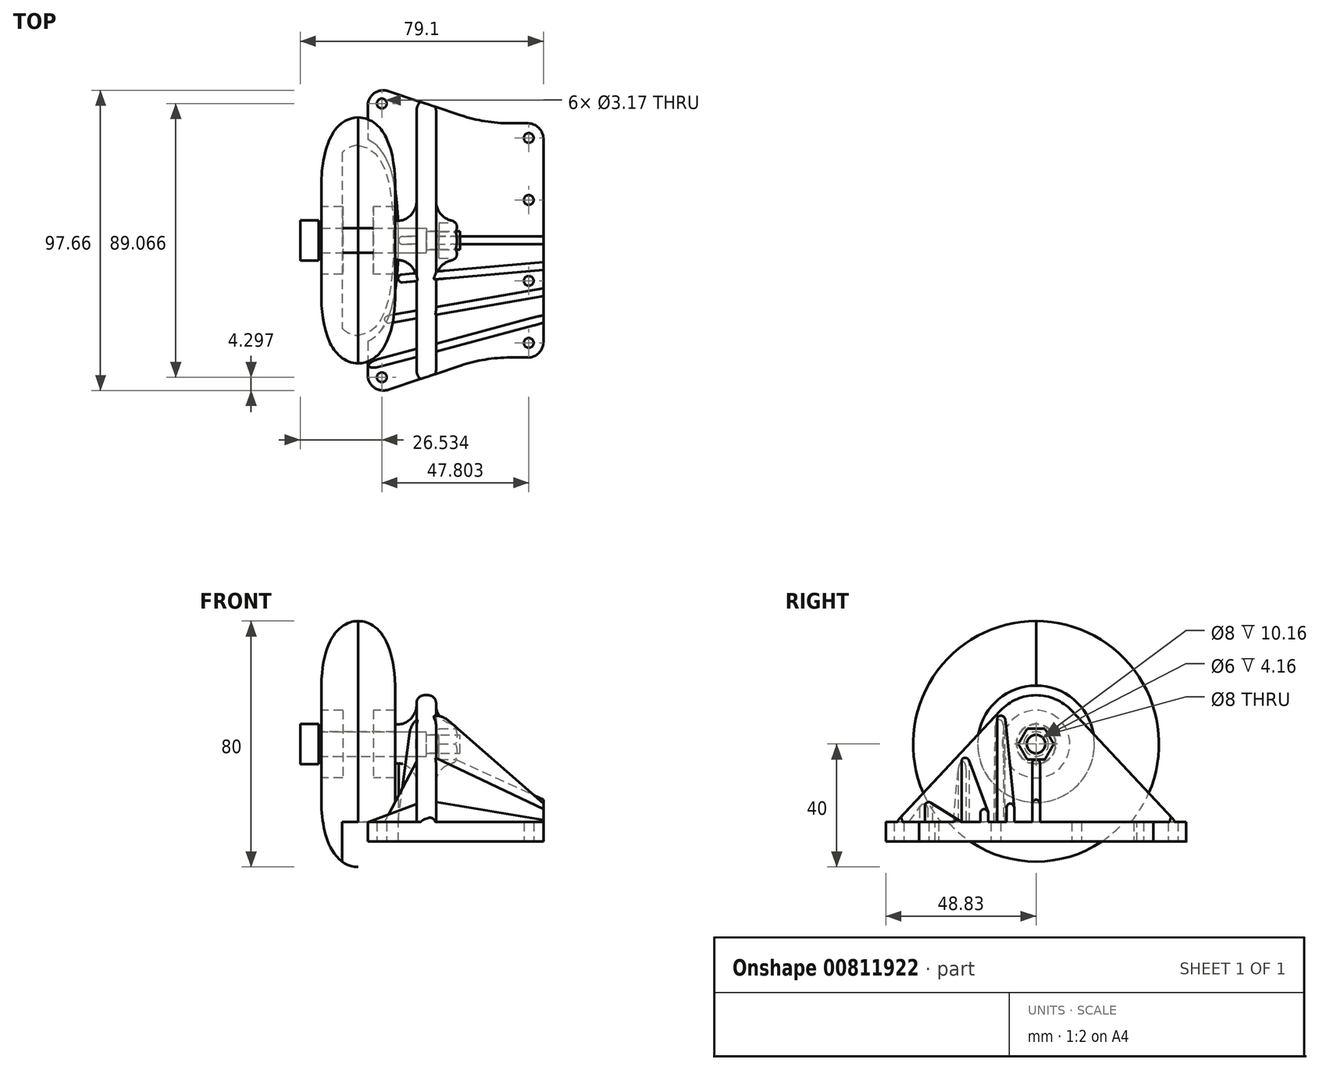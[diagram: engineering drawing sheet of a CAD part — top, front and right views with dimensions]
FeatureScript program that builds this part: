
annotation { "Feature Type Name" : "Feature", "Feature Type Description" : "" }
export const myFeature = defineFeature(function(context is Context, id is Id, definition is map)
    precondition{}
    {
        {
            var Q0;
            Q0=qCreatedBy(makeId("Top.planeOp"),FACE);
            var sketch = newSketch(context, id + "F0", { "sketchPlane" : qUnion([Q0])});
            skLineSegment(sketch, "E0", {"start": v(-19.05, 50.8) * mm, "end": v(-19.05, -50.8) * mm});
            skLineSegment(sketch, "E1", {"start": v(-19.05, -50.8) * mm, "end": v(19.05, -38.1) * mm});
            skLineSegment(sketch, "E2", {"start": v(38.1, -31.75) * mm, "end": v(38.1, 31.75) * mm});
            skLineSegment(sketch, "E3", {"start": v(19.05, 38.1) * mm, "end": v(-19.05, 50.8) * mm});
            skLineSegment(sketch, "E4", {"start": v(19.05, 38.1) * mm, "end": v(38.1, 38.1) * mm});
            skLineSegment(sketch, "E5", {"start": v(38.1, 38.1) * mm, "end": v(38.1, 31.75) * mm});
            skLineSegment(sketch, "E6", {"start": v(19.05, -38.1) * mm, "end": v(38.1, -38.1) * mm});
            skLineSegment(sketch, "E7", {"start": v(38.1, -38.1) * mm, "end": v(38.1, -31.75) * mm});
            skSolve(sketch);
        }
        {
            var Q0;
            Q0=makeQuery(id+"F0.imprint","IMPRINT",FACE,{"disambiguationData":[TD([[makeQuery(id+"F0.imprint","IMPRINT",EDGE,{"derivedFrom":sQuery(id+"F0.wireOp",EDGE,"E0")}),1.0]])]});
            extrude(context, id + "F1", {"entities" : qUnion([Q0]), "depth" : 6.35 * mm});
        }
        {
            var Q0;
            Q0=makeQuery(id+"F1.opExtrude","CAP_FACE",FACE,{"disambiguationData":[OSD([sQuery(id+"F0.wireOp",EDGE,"E0"),sQuery(id+"F0.wireOp",EDGE,"E1"),sQuery(id+"F0.wireOp",EDGE,"E2"),sQuery(id+"F0.wireOp",EDGE,"E3")])],"isStart":false});
            var sketch = newSketch(context, id + "F2", { "sketchPlane" : qUnion([Q0])});
            skLineSegment(sketch, "E8", {"start": v(-3.18, 45.5) * mm, "end": v(-3.17, -45.5) * mm});
            skLineSegment(sketch, "E9", {"start": v(-3.17, -45.5) * mm, "end": v(3.18, -43.4) * mm});
            skLineSegment(sketch, "E10", {"start": v(3.18, -43.4) * mm, "end": v(3.17, 43.4) * mm});
            skLineSegment(sketch, "E11", {"start": v(3.17, 43.4) * mm, "end": v(-3.18, 45.5) * mm});
            skSolve(sketch);
        }
        {
            var Q0;
            Q0=makeQuery(id+"F2.imprint","IMPRINT",FACE,{"disambiguationData":[TD([[makeQuery(id+"F2.imprint","IMPRINT",EDGE,{"derivedFrom":sQuery(id+"F2.wireOp",EDGE,"E8")}),1.0]])]});
            extrude(context, id + "F3", {"entities" : qUnion([Q0]), "operationType" : NewBodyOperationType.ADD, "depth" : 50.8 * mm, "offsetDistance" : 25.4 * mm});
        }
        {
            var Q0;
            Q0=qCreatedBy(makeId("Right.planeOp"),FACE);
            var sketch = newSketch(context, id + "F4", { "sketchPlane" : qUnion([Q0])});
            skArc(sketch, "E12", {"start": v(11.6, 42.6) * mm, "mid": v(0, 47.62) * mm, "end": v(-11.6, 42.6) * mm});
            skLineSegment(sketch, "E13", {"start": v(11.6, 42.6) * mm, "end": v(45.5, 6.35) * mm});
            skLineSegment(sketch, "E14", {"start": v(-11.6, 42.6) * mm, "end": v(-45.5, 6.35) * mm});
            skLineSegment(sketch, "E15", {"start": v(45.5, 6.35) * mm, "end": v(53.44, 6.35) * mm});
            skLineSegment(sketch, "E16", {"start": v(53.44, 6.35) * mm, "end": v(53.44, 59.99) * mm});
            skLineSegment(sketch, "E17", {"start": v(53.44, 59.99) * mm, "end": v(-55.67, 59.99) * mm});
            skLineSegment(sketch, "E18", {"start": v(-55.67, 59.99) * mm, "end": v(-55.67, 6.35) * mm});
            skLineSegment(sketch, "E19", {"start": v(-55.67, 6.35) * mm, "end": v(-45.5, 6.35) * mm});
            skSolve(sketch);
        }
        {
            var Q0;
            Q0=makeQuery(id+"F4.imprint","IMPRINT",FACE,{"disambiguationData":[TD([[makeQuery(id+"F4.imprint","IMPRINT",EDGE,{"derivedFrom":sQuery(id+"F4.wireOp",EDGE,"E12")}),-1.0]])]});
            extrude(context, id + "F5", {"entities" : qUnion([Q0]), "operationType" : NewBodyOperationType.REMOVE, "oppositeDirection" : true, "depth" : 7.11 * mm, "hasSecondDirection" : true, "secondDirectionOppositeDirection" : false, "secondDirectionDepth" : 4.06 * mm});
        }
        {
            var Q0;
            Q0=qCreatedBy(makeId("Right.planeOp"),FACE);
            var sketch = newSketch(context, id + "F6", { "sketchPlane" : qUnion([Q0])});
            skCircle(sketch, "E20", {"center": v(0, 513) * mm, "radius": 63.5 * mm});
            skCircle(sketch, "E21", {"center": v(0, 31.75) * mm, "radius": 6.35 * mm});
            skSolve(sketch);
        }
        {
            var Q0;
            Q0=qSketchRegion(id+"F6",true);
            extrude(context, id + "F7", {"entities" : qUnion([Q0]), "operationType" : NewBodyOperationType.ADD, "depth" : 10.16 * mm, "hasSecondDirection" : true, "secondDirectionOppositeDirection" : true, "secondDirectionDepth" : 10.16 * mm});
        }
        {
            var Q0;
            Q0=makeQuery(id+"F7.boolean.opBoolean","INTERSECT",EDGE,{"derivedFrom":[makeQuery(id+"F3.opExtrude","SWEPT_FACE",FACE,{"disambiguationData":[OSD([sQuery(id+"F2.wireOp",EDGE,"E8")])]}),makeQuery(id+"F7.opExtrude","SWEPT_FACE",FACE,{"disambiguationData":[OSD([sQuery(id+"F6.wireOp",EDGE,"E21")])]})]});
            var Q1;
            Q1=makeQuery(id+"F7.boolean.opBoolean","INTERSECT",EDGE,{"derivedFrom":[makeQuery(id+"F3.opExtrude","SWEPT_FACE",FACE,{"disambiguationData":[OSD([sQuery(id+"F2.wireOp",EDGE,"E10")])]}),makeQuery(id+"F7.opExtrude","SWEPT_FACE",FACE,{"disambiguationData":[OSD([sQuery(id+"F6.wireOp",EDGE,"E21")])]})]});
            fillet(context, id + "F8", {"entities" : qUnion([Q0, Q1]), "radius" : 6.35 * mm, "tangentPropagation" : true, "allowEdgeOverflow" : false});
        }
        {
            var Q0;
            Q0=makeQuery(id+"F5.boolean.opBoolean","INTERSECT",EDGE,{"derivedFrom":[makeQuery(id+"F3.opExtrude","SWEPT_FACE",FACE,{"disambiguationData":[OSD([sQuery(id+"F2.wireOp",EDGE,"E8")])]}),makeQuery(id+"F5.opExtrude","SWEPT_FACE",FACE,{"disambiguationData":[OSD([sQuery(id+"F4.wireOp",EDGE,"E13")])]})]});
            var Q1;
            Q1=makeQuery(id+"F5.boolean.opBoolean","INTERSECT",EDGE,{"derivedFrom":[makeQuery(id+"F3.opExtrude","SWEPT_FACE",FACE,{"disambiguationData":[OSD([sQuery(id+"F2.wireOp",EDGE,"E10")])]}),makeQuery(id+"F5.opExtrude","SWEPT_FACE",FACE,{"disambiguationData":[OSD([sQuery(id+"F4.wireOp",EDGE,"E13")])]})]});
            fillet(context, id + "F9", {"entities" : qUnion([Q0, Q1]), "radius" : 2.54 * mm, "tangentPropagation" : true, "allowEdgeOverflow" : false});
        }
        {
            var Q0;
            Q0=qCreatedBy(makeId("Right.planeOp"),FACE);
            var sketch = newSketch(context, id + "F10", { "sketchPlane" : qUnion([Q0])});
            skCircle(sketch, "E22", {"center": v(0, 31.75) * mm, "radius": 4 * mm});
            skSolve(sketch);
        }
        {
            var Q0;
            Q0=qSketchRegion(id+"F10",true);
            extrude(context, id + "F11", {"entities" : qUnion([Q0]), "operationType" : NewBodyOperationType.REMOVE, "oppositeDirection" : true, "depth" : 25.4 * mm});
        }
        {
            var Q0;
            Q0=makeQuery(id+"F7.opExtrude","CAP_FACE",FACE,{"disambiguationData":[OSD([sQuery(id+"F6.wireOp",EDGE,"E21")])],"isStart":false});
            var sketch = newSketch(context, id + "F12", { "sketchPlane" : qUnion([Q0])});
            skCircle(sketch, "E23.cCircle", {"center": v(0, 31.75) * mm, "radius": 5 * mm, "construction": true});
            skLineSegment(sketch, "E23.0", {"start": v(-2.89, 36.75) * mm, "end": v(2.89, 36.75) * mm});
            skLineSegment(sketch, "E23.1", {"start": v(2.89, 36.75) * mm, "end": v(5.77, 31.75) * mm});
            skLineSegment(sketch, "E23.2", {"start": v(5.77, 31.75) * mm, "end": v(2.89, 26.75) * mm});
            skLineSegment(sketch, "E23.3", {"start": v(2.89, 26.75) * mm, "end": v(-2.89, 26.75) * mm});
            skLineSegment(sketch, "E23.4", {"start": v(-2.89, 26.75) * mm, "end": v(-5.77, 31.75) * mm});
            skLineSegment(sketch, "E23.5", {"start": v(-5.77, 31.75) * mm, "end": v(-2.89, 36.75) * mm});
            skPoint(sketch, "E23.0.midPoint", {"position": v(0, 36.75) * mm});
            skSolve(sketch);
        }
        {
            var Q0;
            Q0=makeQuery(id+"F12.imprint","IMPRINT",FACE,{"disambiguationData":[TD([[makeQuery(id+"F12.imprint","IMPRINT",EDGE,{"derivedFrom":sQuery(id+"F12.wireOp",EDGE,"E23.0")}),-1.0]])]});
            extrude(context, id + "F13", {"entities" : qUnion([Q0]), "operationType" : NewBodyOperationType.REMOVE, "oppositeDirection" : true, "depth" : 6 * mm});
        }
        {
            var Q0;
            Q0=makeQuery(id+"F7.opExtrude","CAP_EDGE",EDGE,{"disambiguationData":[OSD([sQuery(id+"F6.wireOp",EDGE,"E21")])],"isStart":false});
            fillet(context, id + "F14", {"entities" : qUnion([Q0]), "radius" : 2.54 * mm, "tangentPropagation" : true, "allowEdgeOverflow" : false});
        }
        {
            var Q0;
            Q0=makeQuery(id+"F7.opExtrude","SWEPT_BODY",BODY,{"disambiguationData":[OSD([sQuery(id+"F6.wireOp",EDGE,"E20")])]});
            deleteBodies(context, id + "F15", {"entities" : qUnion([Q0])});
        }
        {
            var Q0;
            Q0=qCreatedBy(makeId("Right.planeOp"),FACE);
            var sketch = newSketch(context, id + "F16", { "sketchPlane" : qUnion([Q0])});
            skCircle(sketch, "E24", {"center": v(0, 31.75) * mm, "radius": 3 * mm});
            skSolve(sketch);
        }
        {
            var Q0;
            Q0=qSketchRegion(id+"F16",true);
            extrude(context, id + "F17", {"entities" : qUnion([Q0]), "operationType" : NewBodyOperationType.REMOVE, "depth" : 25.4 * mm});
        }
        {
            var Q0;
            Q0=qCreatedBy(makeId("Front.planeOp"),FACE);
            var sketch = newSketch(context, id + "F18", { "sketchPlane" : qUnion([Q0])});
            skLineSegment(sketch, "E25", {"start": v(0, 31.75) * mm, "end": v(-46.53, 31.75) * mm, "construction": true});
            skLineSegment(sketch, "E26", {"start": v(-35, 35.75) * mm, "end": v(0, 35.75) * mm});
            skLineSegment(sketch, "E27", {"start": v(0, 35.75) * mm, "end": v(0, 34.75) * mm});
            skLineSegment(sketch, "E28", {"start": v(0, 34.75) * mm, "end": v(11, 34.75) * mm});
            skLineSegment(sketch, "E29", {"start": v(11, 34.75) * mm, "end": v(11, 31.75) * mm});
            skLineSegment(sketch, "E30", {"start": v(11, 31.75) * mm, "end": v(-41, 31.75) * mm});
            skLineSegment(sketch, "E31", {"start": v(-35, 35.75) * mm, "end": v(-35, 38.25) * mm});
            skLineSegment(sketch, "E32", {"start": v(-35, 38.25) * mm, "end": v(-41, 38.25) * mm});
            skLineSegment(sketch, "E33", {"start": v(-41, 38.25) * mm, "end": v(-41, 31.75) * mm});
            skSolve(sketch);
        }
        {
            var Q0;
            Q0=makeQuery(id+"F18.imprint","IMPRINT",FACE,{"disambiguationData":[TD([[makeQuery(id+"F18.imprint","IMPRINT",EDGE,{"derivedFrom":sQuery(id+"F18.wireOp",EDGE,"E26")}),-1.0]])]});
            var Q1;
            Q1=sQuery(id+"F18.wireOp",EDGE,"E25");
            revolve(context, id + "F19", {"entities" : qUnion([Q0]), "axis" : qUnion([Q1]), "revolveType" : RevolveType.FULL});
        }
        {
            var Q0;
            Q0=qCreatedBy(makeId("Front.planeOp"),FACE);
            var sketch = newSketch(context, id + "F20", { "sketchPlane" : qUnion([Q0])});
            skLineSegment(sketch, "E34", {"start": v(-51.26, 31.75) * mm, "end": v(0, 31.75) * mm});
            skLineSegment(sketch, "E35", {"start": v(-22.16, 31.75) * mm, "end": v(-22.16, 71.75) * mm, "construction": true});
            skPoint(sketch, "E36", {"position": v(-25.63, 31.75) * mm});
            skLineSegment(sketch, "E37", {"start": v(-22.16, 35.75) * mm, "end": v(-10.16, 35.75) * mm});
            skLineSegment(sketch, "E38", {"start": v(-10.16, 35.75) * mm, "end": v(-10.16, 50.75) * mm});
            skPoint(sketch, "E39.MirrorCS.2.internal.orphan", {"position": v(-34.16, 31.75) * mm});
            skPoint(sketch, "E39.MirrorCS.start.orphan", {"position": v(-22.16, 71.75) * mm});
            skPoint(sketch, "E40.2.internal.orphan", {"position": v(-10.16, 31.75) * mm});
            skFitSpline(sketch, "E41", {"points": [v(-22.16, 71.75) * mm, v(-10.16, 50.75) * mm], "startDerivative": vector(15.26, -0.07) * mm, "endDerivative": vector(1.21, -49.43) * mm});
            skPoint(sketch, "E42.MirrorCS.end.orphan", {"position": v(-34.16, 50.75) * mm});
            skFitSpline(sketch, "E43.MirrorCS", {"points": [v(-22.16, 71.75) * mm, v(-34.16, 50.75) * mm], "startDerivative": vector(-15.26, -0.07) * mm, "endDerivative": vector(-1.21, -49.43) * mm});
            skLineSegment(sketch, "E44.MirrorCS", {"start": v(-34.16, 35.75) * mm, "end": v(-34.16, 50.75) * mm});
            skLineSegment(sketch, "E45.MirrorCS", {"start": v(-22.16, 35.75) * mm, "end": v(-34.16, 35.75) * mm});
            skSolve(sketch);
        }
        {
            var Q0;
            Q0=makeQuery(id+"F20.imprint","IMPRINT",FACE,{"disambiguationData":[TD([[makeQuery(id+"F20.imprint","IMPRINT",EDGE,{"derivedFrom":sQuery(id+"F20.wireOp",EDGE,"E37")}),1.0]])]});
            var Q1;
            Q1=sQuery(id+"F20.wireOp",EDGE,"E34");
            revolve(context, id + "F21", {"entities" : qUnion([Q0]), "axis" : qUnion([Q1]), "revolveType" : RevolveType.FULL});
        }
        {
            var Q0;
            Q0=qCreatedBy(makeId("Front.planeOp"),FACE);
            var sketch = newSketch(context, id + "F22", { "sketchPlane" : qUnion([Q0])});
            skLineSegment(sketch, "E46", {"start": v(-62.06, 31.75) * mm, "end": v(0, 31.75) * mm, "construction": true});
            skLineSegment(sketch, "E47", {"start": v(-10.16, 31.75) * mm, "end": v(-10.16, 42.75) * mm});
            skLineSegment(sketch, "E48", {"start": v(-10.16, 42.75) * mm, "end": v(-17.16, 42.75) * mm});
            skLineSegment(sketch, "E49", {"start": v(-17.16, 42.75) * mm, "end": v(-17.16, 31.75) * mm});
            skLineSegment(sketch, "E50", {"start": v(-17.16, 31.75) * mm, "end": v(-10.16, 31.75) * mm});
            skLineSegment(sketch, "E51", {"start": v(-22.16, 31.75) * mm, "end": v(-22.16, 46.12) * mm, "construction": true});
            skLineSegment(sketch, "E52.MirrorCS", {"start": v(-34.16, 42.75) * mm, "end": v(-27.16, 42.75) * mm});
            skLineSegment(sketch, "E53.MirrorCS", {"start": v(-27.16, 42.75) * mm, "end": v(-27.16, 31.75) * mm});
            skLineSegment(sketch, "E54.MirrorCS", {"start": v(-34.16, 31.75) * mm, "end": v(-34.16, 42.75) * mm});
            skLineSegment(sketch, "E55", {"start": v(-27.16, 31.75) * mm, "end": v(-34.16, 31.75) * mm});
            skSolve(sketch);
        }
        {
            var Q0;
            Q0=qSketchRegion(id+"F22",true);
            var Q1;
            Q1=sQuery(id+"F22.wireOp",EDGE,"E46");
            revolve(context, id + "F23", {"entities" : qUnion([Q0]), "axis" : qUnion([Q1]), "revolveType" : RevolveType.FULL});
        }
        {
            var Q0;
            {var subQ0=sQuery(id+"F0.wireOp",EDGE,"E3");var subQ1=sQuery(id+"F0.wireOp",EDGE,"E1");var subQ2=sQuery(id+"F0.wireOp",EDGE,"E0");Q0=makeQuery(id+"F3.boolean.opBoolean","SPLIT",FACE,{"disambiguationData":[TD([makeQuery(id+"F1.opExtrude","SWEPT_FACE",FACE,{"disambiguationData":[OSD([subQ2])]})])],"derivedFrom":makeQuery(id+"F1.opExtrude","CAP_FACE",FACE,{"disambiguationData":[OSD([subQ2,subQ1,sQuery(id+"F0.wireOp",EDGE,"E2"),subQ0])],"isStart":false})});}
            var sketch = newSketch(context, id + "F24", { "sketchPlane" : qUnion([Q0])});
            skLineSegment(sketch, "E56", {"start": v(-19.05, 32.85) * mm, "end": v(-19.05, -32.85) * mm});
            skFitSpline(sketch, "E57.0", {"points": [v(-22.67, -33.39) * mm, v(-22.46, -33.43) * mm, v(-22.05, -33.49) * mm, v(-21.48, -33.49) * mm, v(-20.97, -33.44) * mm, v(-20.5, -33.35) * mm, v(-20.07, -33.24) * mm, v(-19.65, -33.1) * mm, v(-19.27, -32.95) * mm, v(-18.9, -32.79) * mm, v(-18.56, -32.62) * mm, v(-18.23, -32.43) * mm, v(-17.91, -32.24) * mm, v(-17.5, -31.97) * mm, v(-17.03, -31.62) * mm, v(-16.3, -31.03) * mm, v(-15.49, -30.22) * mm, v(-14.62, -29.2) * mm, v(-13.87, -28.1) * mm, v(-13.21, -26.98) * mm, v(-12.65, -25.84) * mm, v(-12.17, -24.7) * mm, v(-11.76, -23.55) * mm, v(-11.28, -22.02) * mm, v(-10.8, -20.12) * mm, v(-10.34, -17.83) * mm, v(-10, -15.56) * mm, v(-9.63, -12.57) * mm, v(-9.33, -8.85) * mm, v(-9.13, -4.4) * mm, v(-9.07, 0.02) * mm, v(-9.13, 4.46) * mm, v(-9.3, 8.17) * mm, v(-9.52, 11.16) * mm, v(-9.73, 13.4) * mm, v(-10, 15.66) * mm, v(-10.36, 17.92) * mm, v(-10.81, 20.2) * mm, v(-11.4, 22.47) * mm, v(-12.03, 24.37) * mm, v(-12.67, 25.89) * mm, v(-13.24, 27.03) * mm, v(-13.9, 28.15) * mm, v(-14.65, 29.23) * mm, v(-15.52, 30.26) * mm, v(-16.5, 31.2) * mm, v(-17.6, 32.06) * mm, v(-18.66, 32.7) * mm, v(-19.65, 33.11) * mm, v(-20.35, 33.32) * mm, v(-20.98, 33.44) * mm, v(-21.49, 33.49) * mm, v(-22.05, 33.48) * mm, v(-22.46, 33.43) * mm, v(-22.67, 33.39) * mm]});
            skPoint(sketch, "E58.trimOffspring.end.orphan", {"position": v(-22.16, 30.9) * mm});
            skPoint(sketch, "E59.start.orphan", {"position": v(-22.16, -30.9) * mm});
            skLineSegment(sketch, "E60", {"start": v(-19.05, 32.85) * mm, "end": v(-27.36, 32.85) * mm});
            skLineSegment(sketch, "E61", {"start": v(-27.36, 32.85) * mm, "end": v(-27.36, -33.81) * mm});
            skLineSegment(sketch, "E62", {"start": v(-27.36, -33.81) * mm, "end": v(-19.05, -32.85) * mm});
            skSolve(sketch);
        }
        {
            var Q0;
            Q0=makeQuery(id+"F24.imprint","IMPRINT",FACE,{"disambiguationData":[TD([[makeQuery(id+"F24.imprint","IMPRINT",EDGE,{"derivedFrom":sQuery(id+"F24.wireOp",EDGE,"E56")}),-1.0]])]});
            var Q1;
            Q1=makeQuery(id+"F24.imprint","IMPRINT",FACE,{"disambiguationData":[TD([[makeQuery(id+"F24.imprint","IMPRINT",EDGE,{"derivedFrom":sQuery(id+"F24.wireOp",EDGE,"E56")}),1.0]])]});
            extrude(context, id + "F25", {"entities" : qUnion([Q0, Q1]), "operationType" : NewBodyOperationType.REMOVE, "oppositeDirection" : true, "depth" : 25.4 * mm});
        }
        {
            var Q0;
            Q0=qCreatedBy(makeId("Front.planeOp"),FACE);
            var sketch = newSketch(context, id + "F26", { "sketchPlane" : qUnion([Q0])});
            skLineSegment(sketch, "E63", {"start": v(-9.01, 6.35) * mm, "end": v(-9.01, 26.67) * mm});
            skLineSegment(sketch, "E64", {"start": v(-9.01, 26.67) * mm, "end": v(9.85, 26.67) * mm});
            skLineSegment(sketch, "E65", {"start": v(9.85, 26.67) * mm, "end": v(53.98, 6.35) * mm});
            skLineSegment(sketch, "E66", {"start": v(53.98, 6.35) * mm, "end": v(-9.01, 6.35) * mm});
            skSolve(sketch);
        }
        {
            var Q0;
            Q0=makeQuery(id+"F26.imprint","IMPRINT",FACE,{"disambiguationData":[TD([[makeQuery(id+"F26.imprint","IMPRINT",EDGE,{"derivedFrom":sQuery(id+"F26.wireOp",EDGE,"E63")}),-1.0]])]});
            extrude(context, id + "F27", {"entities" : qUnion([Q0]), "operationType" : NewBodyOperationType.ADD, "depth" : 1.27 * mm, "hasSecondDirection" : true, "secondDirectionOppositeDirection" : true, "secondDirectionDepth" : 1.27 * mm});
        }
        {
            var Q0;
            Q0=qCreatedBy(makeId("Top.planeOp"),FACE);
            var sketch = newSketch(context, id + "F28", { "sketchPlane" : qUnion([Q0])});
            skLineSegment(sketch, "E67", {"start": v(-23.06, -52.14) * mm, "end": v(133.35, 0) * mm});
            skLineSegment(sketch, "E68", {"start": v(133.35, 0) * mm, "end": v(-28.84, 0) * mm});
            skLineSegment(sketch, "E69", {"start": v(133.35, 0) * mm, "end": v(-37.86, -14.98) * mm});
            skLineSegment(sketch, "E70", {"start": v(133.35, 0) * mm, "end": v(-37.54, -30.13) * mm});
            skLineSegment(sketch, "E71", {"start": v(133.35, 0) * mm, "end": v(-45.99, -48.05) * mm});
            skSolve(sketch);
        }
        {
            var Q0;
            Q0=sQuery(id+"F28.wireOp",EDGE,"E69");
            cPlane(context, id + "F29", {"entities" : qUnion([Q0]), "cplaneType" : CPlaneType.LINE_ANGLE, "offset" : 25.4 * mm, "angle" : 0 * degree, "width" : 152.4 * mm, "height" : 152.4 * mm});
        }
        {
            var Q0;
            Q0=qCreatedBy(id+"F29.planeOp",FACE);
            var sketch = newSketch(context, id + "F30", { "sketchPlane" : qUnion([Q0])});
            skLineSegment(sketch, "E72", {"start": v(6.12, 39.44) * mm, "end": v(44.18, 6.35) * mm});
            skLineSegment(sketch, "E73", {"start": v(44.18, 6.35) * mm, "end": v(-10.24, 6.35) * mm});
            skLineSegment(sketch, "E74", {"start": v(-10.24, 6.35) * mm, "end": v(-6.43, 35.5) * mm});
            skPoint(sketch, "E75.visualSharp", {"position": v(-6.52, 34.82) * mm});
            skArc(sketch, "E75.filletArc", {"start": v(-3.16, 40.25) * mm, "mid": v(-5.37, 38.27) * mm, "end": v(-6.43, 35.5) * mm});
            skLineSegment(sketch, "E76", {"start": v(1.95, 41) * mm, "end": v(0.46, 41) * mm});
            skLineSegment(sketch, "E77", {"start": v(0.46, 41) * mm, "end": v(-3.16, 40.25) * mm});
            skPoint(sketch, "E78.visualSharp", {"position": v(4.32, 41) * mm});
            skArc(sketch, "E78.filletArc", {"start": v(6.12, 39.44) * mm, "mid": v(4.17, 40.6) * mm, "end": v(1.95, 41) * mm});
            skSolve(sketch);
        }
        {
            var Q0;
            Q0=makeQuery(id+"F30.imprint","IMPRINT",FACE,{"disambiguationData":[TD([[makeQuery(id+"F30.imprint","IMPRINT",EDGE,{"derivedFrom":sQuery(id+"F30.wireOp",EDGE,"E72")}),-1.0]])]});
            extrude(context, id + "F31", {"entities" : qUnion([Q0]), "operationType" : NewBodyOperationType.ADD, "depth" : 1.27 * mm, "hasSecondDirection" : true, "secondDirectionOppositeDirection" : true, "secondDirectionDepth" : 1.27 * mm});
        }
        {
            var Q0;
            Q0=sQuery(id+"F28.wireOp",EDGE,"E70");
            cPlane(context, id + "F32", {"entities" : qUnion([Q0]), "cplaneType" : CPlaneType.LINE_ANGLE, "offset" : 25.4 * mm, "angle" : 0 * degree, "width" : 152.4 * mm, "height" : 152.4 * mm});
        }
        {
            var Q0;
            Q0=qCreatedBy(id+"F32.planeOp",FACE);
            var sketch = newSketch(context, id + "F33", { "sketchPlane" : qUnion([Q0])});
            skLineSegment(sketch, "E79", {"start": v(43.53, 6.35) * mm, "end": v(-17.77, 6.35) * mm});
            skLineSegment(sketch, "E80", {"start": v(-17.77, 6.35) * mm, "end": v(-6.14, 28.2) * mm});
            skLineSegment(sketch, "E81", {"start": v(-6.14, 28.2) * mm, "end": v(-2.9, 28.2) * mm});
            skLineSegment(sketch, "E82", {"start": v(-2.9, 28.2) * mm, "end": v(43.53, 6.35) * mm});
            skSolve(sketch);
        }
        {
            var Q0;
            Q0=makeQuery(id+"F33.imprint","IMPRINT",FACE,{"disambiguationData":[TD([[makeQuery(id+"F33.imprint","IMPRINT",EDGE,{"derivedFrom":sQuery(id+"F33.wireOp",EDGE,"E79")}),-1.0]])]});
            extrude(context, id + "F34", {"entities" : qUnion([Q0]), "operationType" : NewBodyOperationType.ADD, "depth" : 1.27 * mm, "hasSecondDirection" : true, "secondDirectionOppositeDirection" : true, "secondDirectionDepth" : 1.27 * mm});
        }
        {
            var Q0;
            Q0=sQuery(id+"F28.wireOp",EDGE,"E71");
            cPlane(context, id + "F35", {"entities" : qUnion([Q0]), "cplaneType" : CPlaneType.LINE_ANGLE, "offset" : 25.4 * mm, "angle" : 0 * degree, "width" : 152.4 * mm, "height" : 152.4 * mm});
        }
        {
            var Q0;
            Q0=qCreatedBy(id+"F35.planeOp",FACE);
            var sketch = newSketch(context, id + "F36", { "sketchPlane" : qUnion([Q0])});
            skLineSegment(sketch, "E83", {"start": v(-28.7, 6.35) * mm, "end": v(-10.05, 13.08) * mm});
            skLineSegment(sketch, "E84", {"start": v(-10.05, 13.08) * mm, "end": v(-7.43, 13.08) * mm});
            skLineSegment(sketch, "E85", {"start": v(-7.43, 13.08) * mm, "end": v(34.6, 6.35) * mm});
            skLineSegment(sketch, "E86", {"start": v(34.6, 6.35) * mm, "end": v(-28.7, 6.35) * mm});
            skSolve(sketch);
        }
        {
            var Q0;
            Q0=makeQuery(id+"F36.imprint","IMPRINT",FACE,{"disambiguationData":[TD([[makeQuery(id+"F36.imprint","IMPRINT",EDGE,{"derivedFrom":sQuery(id+"F36.wireOp",EDGE,"E83")}),-1.0]])]});
            extrude(context, id + "F37", {"entities" : qUnion([Q0]), "operationType" : NewBodyOperationType.ADD, "depth" : 1.27 * mm, "hasSecondDirection" : true, "secondDirectionOppositeDirection" : true, "secondDirectionDepth" : 1.27 * mm});
        }
        {
            var Q0;
            Q0=qCreatedBy(makeId("Top.planeOp"),FACE);
            var sketch = newSketch(context, id + "F38", { "sketchPlane" : qUnion([Q0])});
            skLineSegment(sketch, "E87", {"start": v(-19.05, 47.14) * mm, "end": v(-19.05, -47.14) * mm});
            skLineSegment(sketch, "E88", {"start": v(-12.36, 48.57) * mm, "end": v(-22.52, 51.96) * mm});
            skLineSegment(sketch, "E89", {"start": v(38.1, 70.87) * mm, "end": v(38.1, -40.92) * mm});
            skLineSegment(sketch, "E90", {"start": v(-22.52, -51.96) * mm, "end": v(-12.36, -48.57) * mm});
            skPoint(sketch, "E91.visualSharp", {"position": v(-19.05, 50.8) * mm});
            skArc(sketch, "E91.filletArc", {"start": v(-19.05, 47.14) * mm, "mid": v(-20, 50.1) * mm, "end": v(-22.52, 51.96) * mm});
            skPoint(sketch, "E92.visualSharp", {"position": v(-19.05, -50.8) * mm});
            skArc(sketch, "E92.filletArc", {"start": v(-22.52, -51.96) * mm, "mid": v(-20, -50.1) * mm, "end": v(-19.05, -47.14) * mm});
            skLineSegment(sketch, "E93", {"start": v(-19.05, 43.75) * mm, "end": v(-19.05, 35.1) * mm});
            skLineSegment(sketch, "E94", {"start": v(-19.05, 35.1) * mm, "end": v(-54.33, 35.1) * mm});
            skLineSegment(sketch, "E95", {"start": v(-54.33, 35.1) * mm, "end": v(-54.33, 78.4) * mm});
            skLineSegment(sketch, "E96", {"start": v(-54.33, 78.4) * mm, "end": v(38.1, 70.87) * mm});
            skArc(sketch, "E97.filletArc", {"start": v(-12.36, 48.57) * mm, "mid": v(-16.94, 47.87) * mm, "end": v(-19.05, 43.75) * mm});
            skLineSegment(sketch, "E98", {"start": v(-19.05, -43.75) * mm, "end": v(-19.05, -36.43) * mm});
            skLineSegment(sketch, "E99", {"start": v(-19.05, -36.43) * mm, "end": v(-56.87, -36.43) * mm});
            skLineSegment(sketch, "E100", {"start": v(-56.87, -36.43) * mm, "end": v(-56.87, -71.2) * mm});
            skLineSegment(sketch, "E101", {"start": v(-56.87, -71.2) * mm, "end": v(38.1, -40.92) * mm});
            skArc(sketch, "E102.filletArc", {"start": v(-19.05, -43.75) * mm, "mid": v(-16.94, -47.87) * mm, "end": v(-12.36, -48.57) * mm});
            skSolve(sketch);
        }
        {
            var Q0;
            Q0=makeQuery(id+"F38.imprint","IMPRINT",FACE,{"disambiguationData":[TD([[makeQuery(id+"F38.imprint","IMPRINT",EDGE,{"derivedFrom":sQuery(id+"F38.wireOp",EDGE,"E87")}),1.0]])]});
            extrude(context, id + "F39", {"entities" : qUnion([Q0]), "operationType" : NewBodyOperationType.REMOVE, "depth" : 25.4 * mm});
        }
        {
            var Q0;
            Q0=qCreatedBy(makeId("Top.planeOp"),FACE);
            var sketch = newSketch(context, id + "F40", { "sketchPlane" : qUnion([Q0])});
            skCircle(sketch, "E103", {"center": v(-14.47, 44.53) * mm, "radius": 1.59 * mm});
            skCircle(sketch, "E104", {"center": v(33.34, 33.34) * mm, "radius": 1.59 * mm});
            skCircle(sketch, "E105", {"center": v(33.34, 13.15) * mm, "radius": 1.59 * mm});
            skLineSegment(sketch, "E106", {"start": v(-47.45, 0) * mm, "end": v(55.73, 0) * mm, "construction": true});
            skCircle(sketch, "E107.MirrorC", {"center": v(-14.47, -44.53) * mm, "radius": 1.59 * mm});
            skCircle(sketch, "E108.MirrorC", {"center": v(33.34, -33.34) * mm, "radius": 1.59 * mm});
            skCircle(sketch, "E109.MirrorC", {"center": v(33.34, -13.15) * mm, "radius": 1.59 * mm});
            skSolve(sketch);
        }
        {
            var Q0;
            Q0=qSketchRegion(id+"F40",true);
            extrude(context, id + "F41", {"entities" : qUnion([Q0]), "operationType" : NewBodyOperationType.REMOVE, "depth" : 25.4 * mm});
        }
        {
            var Q0;
            Q0=qCreatedBy(makeId("Top.planeOp"),FACE);
            var sketch = newSketch(context, id + "F42", { "sketchPlane" : qUnion([Q0])});
            skLineSegment(sketch, "E110", {"start": v(38.1, 38.22) * mm, "end": v(38.1, -45.48) * mm});
            skLineSegment(sketch, "E111", {"start": v(38.1, -45.48) * mm, "end": v(62.17, -45.48) * mm});
            skLineSegment(sketch, "E112", {"start": v(62.17, -45.48) * mm, "end": v(51.52, 37.8) * mm});
            skLineSegment(sketch, "E113", {"start": v(51.52, 37.8) * mm, "end": v(38.1, 38.22) * mm});
            skSolve(sketch);
        }
        {
            var Q0;
            Q0=makeQuery(id+"F42.imprint","IMPRINT",FACE,{"disambiguationData":[TD([[makeQuery(id+"F42.imprint","IMPRINT",EDGE,{"derivedFrom":sQuery(id+"F42.wireOp",EDGE,"E110")}),1.0]])]});
            extrude(context, id + "F43", {"entities" : qUnion([Q0]), "operationType" : NewBodyOperationType.REMOVE, "depth" : 22.35 * mm});
        }
        {
            var Q0;
            Q0=makeQuery(id+"F1.opExtrude","SWEPT_EDGE",EDGE,{"disambiguationData":[OSD([sQuery(id+"F0.wireOp",EDGE,"E6"),sQuery(id+"F0.wireOp",EDGE,"E7")])]});
            var Q1;
            Q1=makeQuery(id+"F1.opExtrude","SWEPT_EDGE",EDGE,{"disambiguationData":[OSD([sQuery(id+"F0.wireOp",EDGE,"E4"),sQuery(id+"F0.wireOp",EDGE,"E5")])]});
            fillet(context, id + "F44", {"entities" : qUnion([Q0, Q1]), "radius" : 5.08 * mm, "tangentPropagation" : true, "allowEdgeOverflow" : false});
        }
        {
            var Q0;
            Q0=makeQuery(id+"F1.opExtrude","SWEPT_EDGE",EDGE,{"disambiguationData":[OSD([sQuery(id+"F0.wireOp",EDGE,"E3"),sQuery(id+"F0.wireOp",EDGE,"E4")])]});
            var Q1;
            Q1=makeQuery(id+"F1.opExtrude","SWEPT_EDGE",EDGE,{"disambiguationData":[OSD([sQuery(id+"F0.wireOp",EDGE,"E1"),sQuery(id+"F0.wireOp",EDGE,"E6")])]});
            fillet(context, id + "F45", {"entities" : qUnion([Q0, Q1]), "radius" : 50.8 * mm, "tangentPropagation" : true, "allowEdgeOverflow" : false});
        }
        {
            var Q0;
            Q0=makeQuery(id+"F27.opExtrude","CAP_EDGE",EDGE,{"disambiguationData":[OSD([sQuery(id+"F26.wireOp",EDGE,"E65")])],"isStart":false});
            var Q1;
            Q1=makeQuery(id+"F27.opExtrude","CAP_EDGE",EDGE,{"disambiguationData":[OSD([sQuery(id+"F26.wireOp",EDGE,"E65")])],"isStart":true});
            var Q2;
            Q2=makeQuery(id+"F31.opExtrude","CAP_EDGE",EDGE,{"disambiguationData":[OSD([sQuery(id+"F30.wireOp",EDGE,"E72")])],"isStart":true});
            var Q3;
            Q3=makeQuery(id+"F31.opExtrude","CAP_EDGE",EDGE,{"disambiguationData":[OSD([sQuery(id+"F30.wireOp",EDGE,"E72")])],"isStart":false});
            var Q4;
            Q4=makeQuery(id+"F31.opExtrude","CAP_EDGE",EDGE,{"disambiguationData":[OSD([sQuery(id+"F30.wireOp",EDGE,"E75.filletArc")])],"isStart":false});
            var Q5;
            Q5=makeQuery(id+"F31.opExtrude","CAP_EDGE",EDGE,{"disambiguationData":[OSD([sQuery(id+"F30.wireOp",EDGE,"E75.filletArc")])],"isStart":true});
            var Q6;
            Q6=makeQuery(id+"F34.opExtrude","CAP_EDGE",EDGE,{"disambiguationData":[OSD([sQuery(id+"F33.wireOp",EDGE,"E82")])],"isStart":false});
            var Q7;
            Q7=makeQuery(id+"F34.opExtrude","CAP_EDGE",EDGE,{"disambiguationData":[OSD([sQuery(id+"F33.wireOp",EDGE,"E82")])],"isStart":true});
            var Q8;
            Q8=makeQuery(id+"F34.opExtrude","CAP_EDGE",EDGE,{"disambiguationData":[OSD([sQuery(id+"F33.wireOp",EDGE,"E80")])],"isStart":false});
            var Q9;
            Q9=makeQuery(id+"F34.opExtrude","CAP_EDGE",EDGE,{"disambiguationData":[OSD([sQuery(id+"F33.wireOp",EDGE,"E80")])],"isStart":true});
            var Q10;
            Q10=makeQuery(id+"F37.opExtrude","CAP_EDGE",EDGE,{"disambiguationData":[OSD([sQuery(id+"F36.wireOp",EDGE,"E83")])],"isStart":false});
            var Q11;
            Q11=makeQuery(id+"F37.opExtrude","CAP_EDGE",EDGE,{"disambiguationData":[OSD([sQuery(id+"F36.wireOp",EDGE,"E83")])],"isStart":true});
            var Q12;
            Q12=makeQuery(id+"F37.opExtrude","CAP_EDGE",EDGE,{"disambiguationData":[OSD([sQuery(id+"F36.wireOp",EDGE,"E85")])],"isStart":false});
            var Q13;
            Q13=makeQuery(id+"F37.opExtrude","CAP_EDGE",EDGE,{"disambiguationData":[OSD([sQuery(id+"F36.wireOp",EDGE,"E85")])],"isStart":true});
            var Q14;
            Q14=makeQuery(id+"FzpeDoiq8tc86xp_5.1.F31.opExtrude","CAP_EDGE",EDGE,{"disambiguationData":[OSD([sQuery(id+"F30.wireOp",EDGE,"E72")])],"isStart":true});
            var Q15;
            Q15=makeQuery(id+"FzpeDoiq8tc86xp_5.1.F31.opExtrude","CAP_EDGE",EDGE,{"disambiguationData":[OSD([sQuery(id+"F30.wireOp",EDGE,"E72")])],"isStart":false});
            var Q16;
            Q16=makeQuery(id+"FzpeDoiq8tc86xp_5.1.F34.opExtrude","CAP_EDGE",EDGE,{"disambiguationData":[OSD([sQuery(id+"F33.wireOp",EDGE,"E82")])],"isStart":true});
            var Q17;
            Q17=makeQuery(id+"FzpeDoiq8tc86xp_5.1.F34.opExtrude","CAP_EDGE",EDGE,{"disambiguationData":[OSD([sQuery(id+"F33.wireOp",EDGE,"E82")])],"isStart":false});
            var Q18;
            Q18=makeQuery(id+"FzpeDoiq8tc86xp_5.1.F37.opExtrude","CAP_EDGE",EDGE,{"disambiguationData":[OSD([sQuery(id+"F36.wireOp",EDGE,"E85")])],"isStart":true});
            var Q19;
            Q19=makeQuery(id+"FzpeDoiq8tc86xp_5.1.F37.opExtrude","CAP_EDGE",EDGE,{"disambiguationData":[OSD([sQuery(id+"F36.wireOp",EDGE,"E85")])],"isStart":false});
            var Q20;
            Q20=makeQuery(id+"F27.opExtrude","CAP_EDGE",EDGE,{"disambiguationData":[OSD([sQuery(id+"F26.wireOp",EDGE,"E63")])],"isStart":false});
            var Q21;
            Q21=makeQuery(id+"FzpeDoiq8tc86xp_5.1.F31.opExtrude","CAP_EDGE",EDGE,{"disambiguationData":[OSD([sQuery(id+"F30.wireOp",EDGE,"E74")])],"isStart":true});
            var Q22;
            Q22=makeQuery(id+"FzpeDoiq8tc86xp_5.1.F31.opExtrude","CAP_EDGE",EDGE,{"disambiguationData":[OSD([sQuery(id+"F30.wireOp",EDGE,"E74")])],"isStart":false});
            var Q23;
            Q23=makeQuery(id+"FzpeDoiq8tc86xp_5.1.F34.opExtrude","CAP_EDGE",EDGE,{"disambiguationData":[OSD([sQuery(id+"F33.wireOp",EDGE,"E80")])],"isStart":true});
            var Q24;
            Q24=makeQuery(id+"FzpeDoiq8tc86xp_5.1.F34.opExtrude","CAP_EDGE",EDGE,{"disambiguationData":[OSD([sQuery(id+"F33.wireOp",EDGE,"E80")])],"isStart":false});
            var Q25;
            Q25=makeQuery(id+"FzpeDoiq8tc86xp_5.1.F37.opExtrude","CAP_EDGE",EDGE,{"disambiguationData":[OSD([sQuery(id+"F36.wireOp",EDGE,"E83")])],"isStart":true});
            var Q26;
            Q26=makeQuery(id+"F27.opExtrude","CAP_EDGE",EDGE,{"disambiguationData":[OSD([sQuery(id+"F26.wireOp",EDGE,"E63")])],"isStart":true});
            fillet(context, id + "F46", {"entities" : qUnion([Q0, Q1, Q2, Q3, Q4, Q5, Q6, Q7, Q8, Q9, Q10, Q11, Q12, Q13, Q14, Q15, Q16, Q17, Q18, Q19, Q20, Q21, Q22, Q23, Q24, Q25, Q26]), "radius" : 1.27 * mm, "tangentPropagation" : true, "allowEdgeOverflow" : false});
        }
    });
